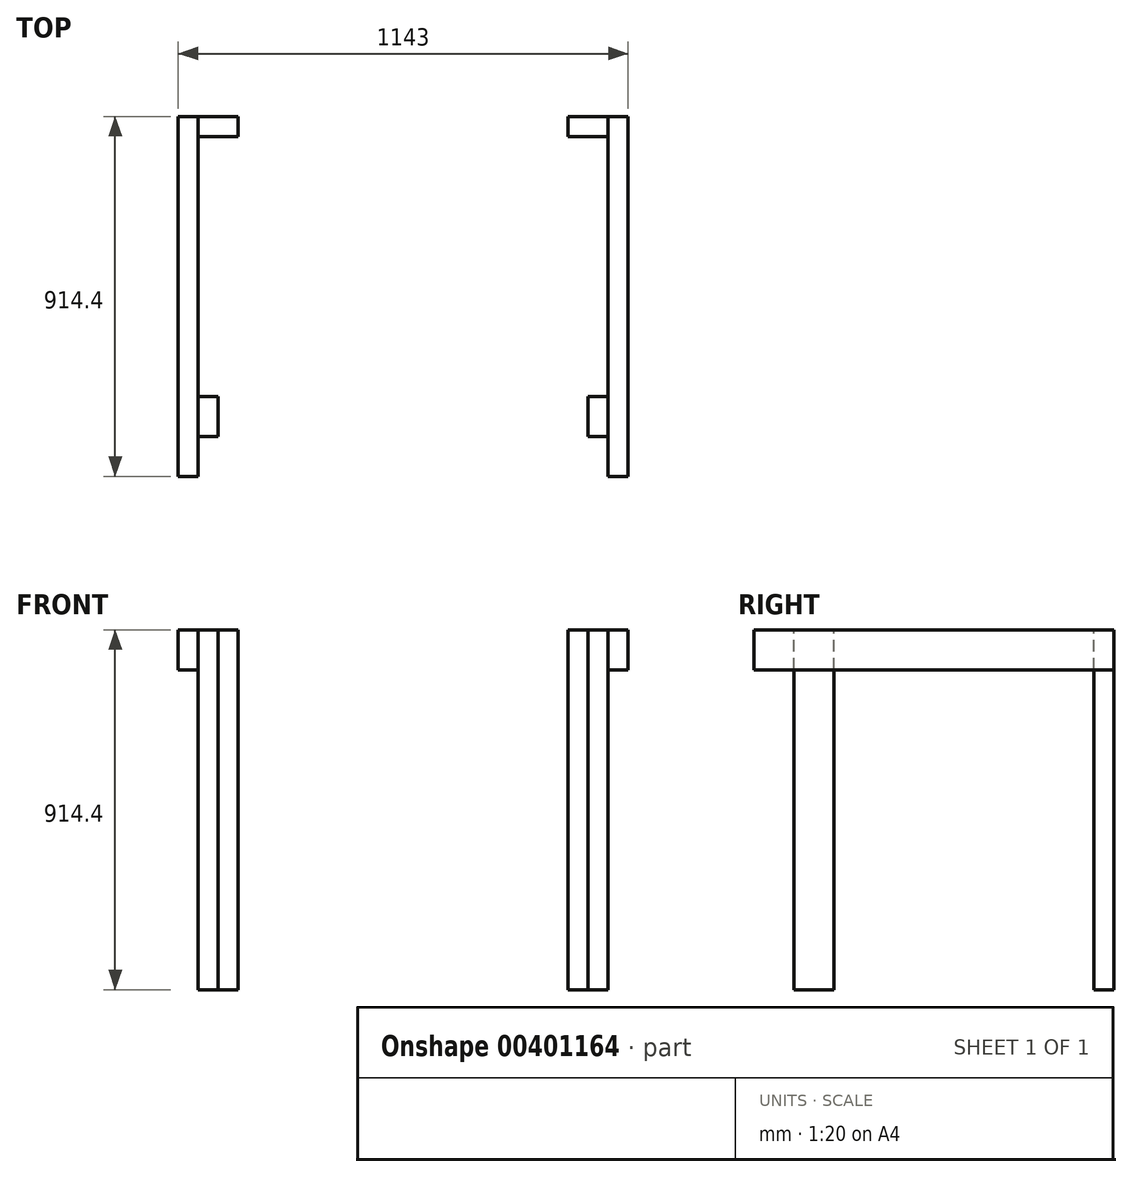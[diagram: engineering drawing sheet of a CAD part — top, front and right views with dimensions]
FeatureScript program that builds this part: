
annotation { "Feature Type Name" : "Feature", "Feature Type Description" : "" }
export const myFeature = defineFeature(function(context is Context, id is Id, definition is map)
    precondition{}
    {
        {
            var Q0;
            Q0=qCreatedBy(makeId("Top.planeOp"),FACE);
            var sketch = newSketch(context, id + "F0", { "sketchPlane" : qUnion([Q0])});
            skLineSegment(sketch, "E0.bottom", {"start": v(0, 101.6) * mm, "end": v(101.6, 101.6) * mm});
            skLineSegment(sketch, "E0.top", {"start": v(0, 0) * mm, "end": v(101.6, 0) * mm});
            skLineSegment(sketch, "E0.left", {"start": v(0, 101.6) * mm, "end": v(0, 0) * mm});
            skLineSegment(sketch, "E0.right", {"start": v(101.6, 101.6) * mm, "end": v(101.6, 0) * mm});
            skSolve(sketch);
        }
        {
            var Q0;
            Q0=qCreatedBy(makeId("Front.planeOp"),FACE);
            var sketch = newSketch(context, id + "F1", { "sketchPlane" : qUnion([Q0])});
            skLineSegment(sketch, "E1.bottom", {"start": v(0, 914.4) * mm, "end": v(50.8, 914.4) * mm});
            skLineSegment(sketch, "E1.top", {"start": v(0, 812.8) * mm, "end": v(50.8, 812.8) * mm});
            skLineSegment(sketch, "E1.left", {"start": v(0, 914.4) * mm, "end": v(0, 812.8) * mm});
            skLineSegment(sketch, "E1.right", {"start": v(50.8, 914.4) * mm, "end": v(50.8, 812.8) * mm});
            skLineSegment(sketch, "E2.bottom", {"start": v(1092.2, 914.4) * mm, "end": v(1143, 914.4) * mm});
            skLineSegment(sketch, "E2.top", {"start": v(1092.2, 812.8) * mm, "end": v(1143, 812.8) * mm});
            skLineSegment(sketch, "E2.left", {"start": v(1092.2, 914.4) * mm, "end": v(1092.2, 812.8) * mm});
            skLineSegment(sketch, "E2.right", {"start": v(1143, 914.4) * mm, "end": v(1143, 812.8) * mm});
            skSolve(sketch);
        }
        {
            var Q0;
            Q0 = qSketchRegion(id + "F1", true);
            extrude(context, id + "F2", {"entities" : qUnion([Q0]), "depth" : 914.4 * mm});
        }
        {
            var Q0;
            Q0=makeQuery(id+"F2.opExtrude","SWEPT_FACE",FACE,{"disambiguationData":[OSD([sQuery(id+"F1.wireOp",EDGE,"E1.bottom")])]});
            var sketch = newSketch(context, id + "F3", { "sketchPlane" : qUnion([Q0])});
            skSolve(sketch);
        }
        {
            var Q0;
            {var subQ0=sQuery(id+"F1.wireOp",EDGE,"E1.bottom");Q0=makeQuery(id+"F3.imprint","IMPRINT",FACE,{"disambiguationData":[TD([[makeQuery(id+"F3.imprint","IMPRINT",EDGE,{"derivedFrom":makeQuery(id+"F2.opExtrude","CAP_EDGE",EDGE,{"disambiguationData":[OSD([subQ0])],"isStart":true})}),-1.0]])]});}
            var sketch = newSketch(context, id + "F4", { "sketchPlane" : qUnion([Q0])});
            skLineSegment(sketch, "E3.bottom", {"start": v(50.8, 0) * mm, "end": v(152.4, 0) * mm});
            skLineSegment(sketch, "E3.top", {"start": v(50.8, -50.8) * mm, "end": v(152.4, -50.8) * mm});
            skLineSegment(sketch, "E3.left", {"start": v(50.8, 0) * mm, "end": v(50.8, -50.8) * mm});
            skLineSegment(sketch, "E3.right", {"start": v(152.4, 0) * mm, "end": v(152.4, -50.8) * mm});
            skLineSegment(sketch, "E4.bottom", {"start": v(1092.2, 0) * mm, "end": v(990.6, 0) * mm});
            skLineSegment(sketch, "E4.top", {"start": v(1092.2, -50.8) * mm, "end": v(990.6, -50.8) * mm});
            skLineSegment(sketch, "E4.left", {"start": v(1092.2, 0) * mm, "end": v(1092.2, -50.8) * mm});
            skLineSegment(sketch, "E4.right", {"start": v(990.6, 0) * mm, "end": v(990.6, -50.8) * mm});
            skLineSegment(sketch, "E5.bottom", {"start": v(50.8, -711.2) * mm, "end": v(101.6, -711.2) * mm});
            skLineSegment(sketch, "E5.top", {"start": v(50.8, -812.8) * mm, "end": v(101.6, -812.8) * mm});
            skLineSegment(sketch, "E5.left", {"start": v(50.8, -711.2) * mm, "end": v(50.8, -812.8) * mm});
            skLineSegment(sketch, "E5.right", {"start": v(101.6, -711.2) * mm, "end": v(101.6, -812.8) * mm});
            skLineSegment(sketch, "E6.bottom", {"start": v(1092.2, -711.2) * mm, "end": v(1041.4, -711.2) * mm});
            skLineSegment(sketch, "E6.top", {"start": v(1092.2, -812.8) * mm, "end": v(1041.4, -812.8) * mm});
            skLineSegment(sketch, "E6.left", {"start": v(1092.2, -711.2) * mm, "end": v(1092.2, -812.8) * mm});
            skLineSegment(sketch, "E6.right", {"start": v(1041.4, -711.2) * mm, "end": v(1041.4, -812.8) * mm});
            skSolve(sketch);
        }
        {
            var Q0;
            Q0 = qSketchRegion(id + "F4", true);
            extrude(context, id + "F5", {"entities" : qUnion([Q0]), "oppositeDirection" : true, "depth" : 914.4 * mm});
        }
    });
